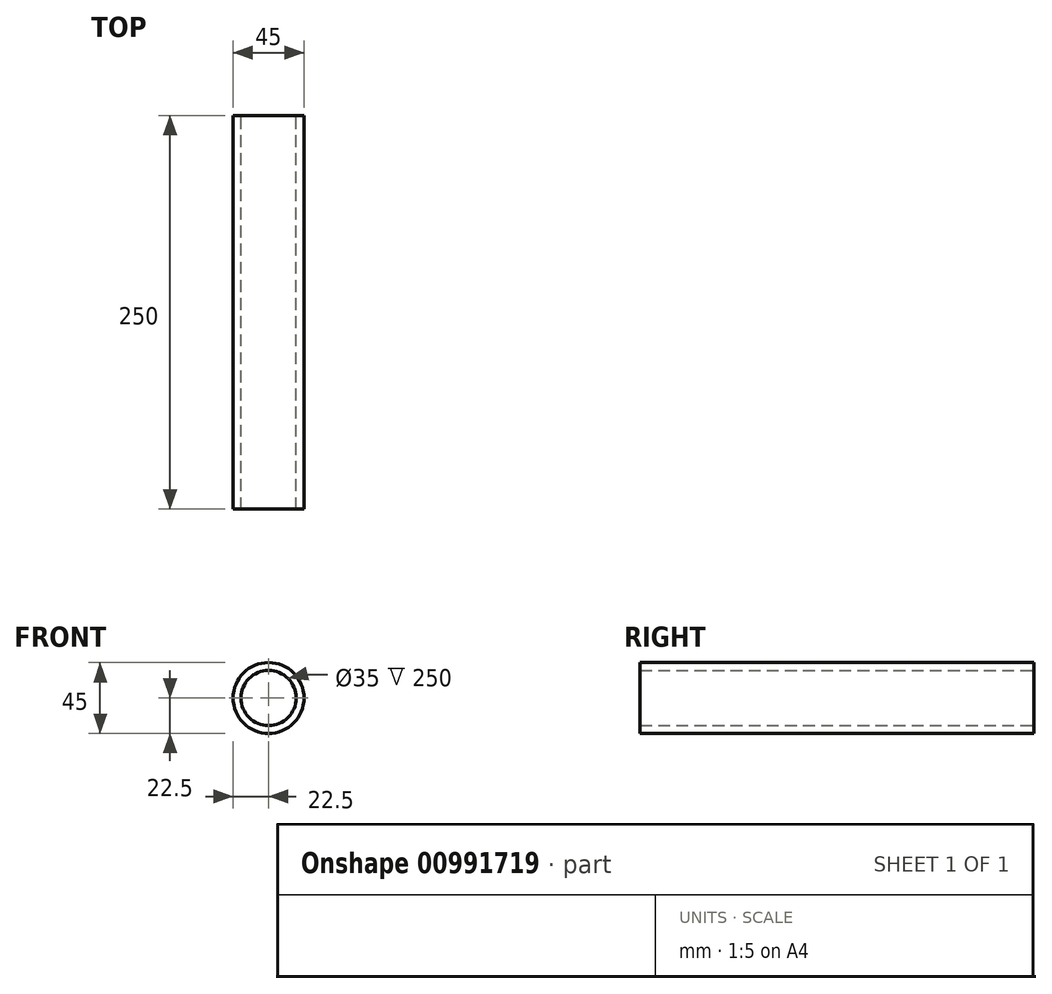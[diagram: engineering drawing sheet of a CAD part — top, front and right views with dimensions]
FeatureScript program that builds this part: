
annotation { "Feature Type Name" : "Feature", "Feature Type Description" : "" }
export const myFeature = defineFeature(function(context is Context, id is Id, definition is map)
    precondition{}
    {
        {
            var Q0;
            Q0=qCreatedBy(makeId("Front.planeOp"),FACE);
            var sketch = newSketch(context, id + "F0", { "sketchPlane" : qUnion([Q0])});
            skCircle(sketch, "E0", {"center": v(0, 0) * mm, "radius": 22.5 * mm});
            skCircle(sketch, "E1", {"center": v(0, 0) * mm, "radius": 17.5 * mm});
            skSolve(sketch);
        }
        {
            var Q0;
            Q0=makeQuery(id+"F0.imprint","IMPRINT",FACE,{"disambiguationData":[TD([[makeQuery(id+"F0.imprint","IMPRINT",EDGE,{"derivedFrom":sQuery(id+"F0.wireOp",EDGE,"E0")}),1.0]])]});
            extrude(context, id + "F1", {"entities" : qUnion([Q0]), "depth" : 250 * mm, "offsetDistance" : 25 * mm});
        }
    });
